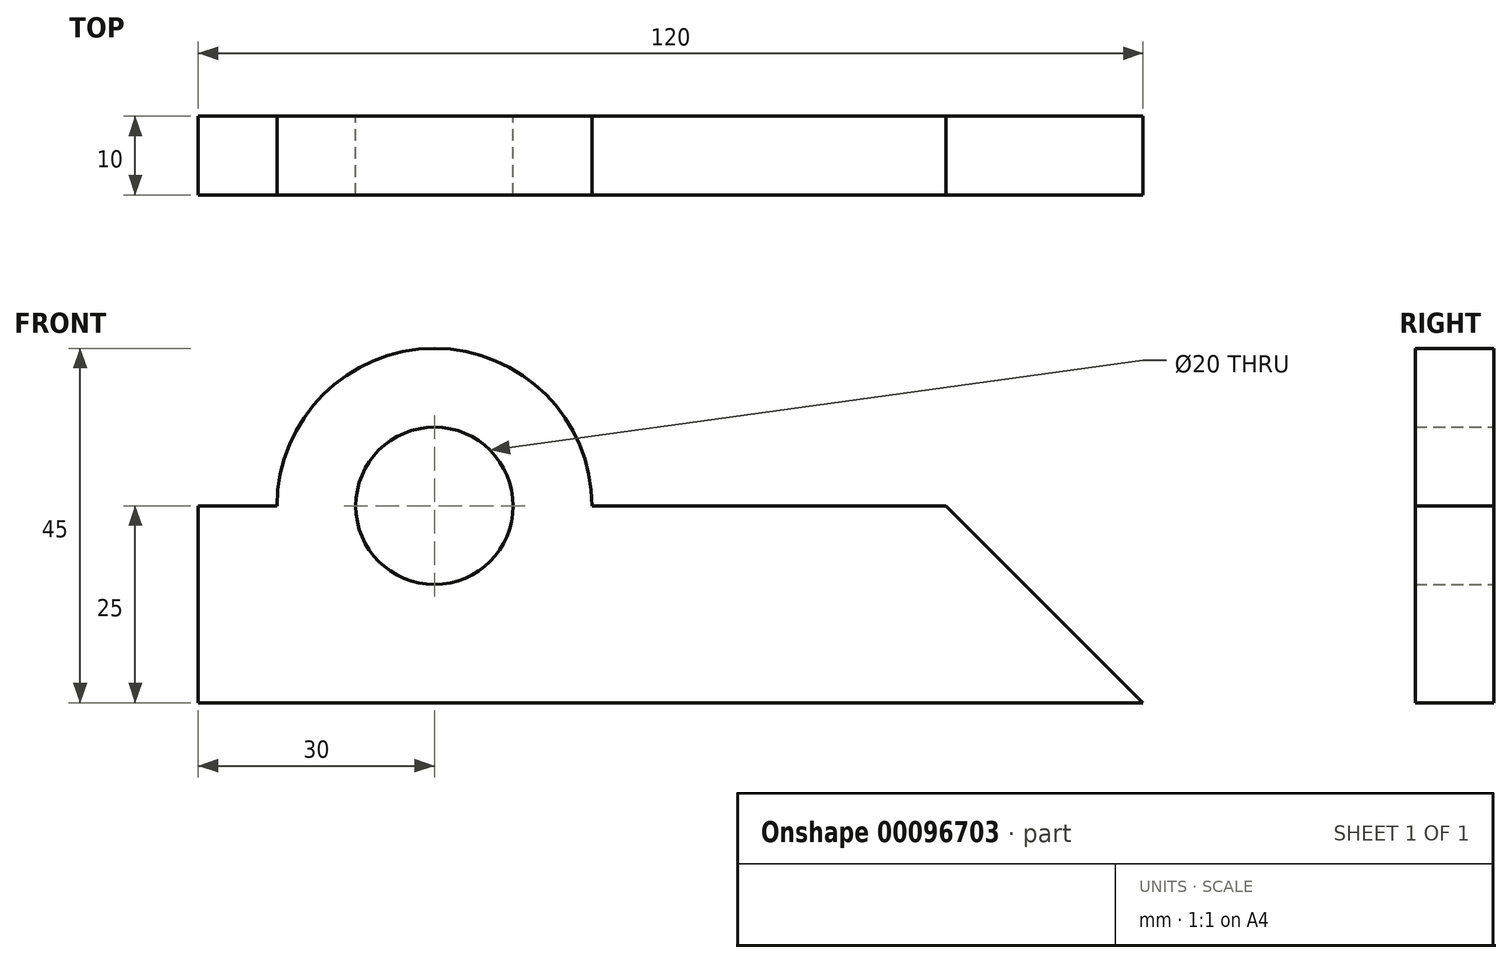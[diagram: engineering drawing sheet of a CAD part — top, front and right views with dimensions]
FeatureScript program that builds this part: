
annotation { "Feature Type Name" : "Feature", "Feature Type Description" : "" }
export const myFeature = defineFeature(function(context is Context, id is Id, definition is map)
    precondition{}
    {
        {
            var Q0;
            Q0=qCreatedBy(makeId("Front.planeOp"),FACE);
            var sketch = newSketch(context, id + "F0", { "sketchPlane" : qUnion([Q0])});
            skLineSegment(sketch, "E0", {"start": v(0, 0) * mm, "end": v(0, 25) * mm});
            skLineSegment(sketch, "E1", {"start": v(0, 25) * mm, "end": v(0, 0) * mm});
            skLineSegment(sketch, "E2", {"start": v(120, 0) * mm, "end": v(95, 25) * mm});
            skLineSegment(sketch, "E3", {"start": v(95, 25) * mm, "end": v(50, 25) * mm});
            skLineSegment(sketch, "E4", {"start": v(0, 25) * mm, "end": v(10, 25) * mm});
            skArc(sketch, "E5", {"start": v(50, 25) * mm, "mid": v(30, 45) * mm, "end": v(10, 25) * mm});
            skLineSegment(sketch, "E6", {"start": v(0, 0) * mm, "end": v(120, 0) * mm});
            skCircle(sketch, "E7", {"center": v(30, 25) * mm, "radius": 10 * mm});
            skSolve(sketch);
        }
        {
            var Q0;
            Q0 = qSketchRegion(id + "F0", true);
            extrude(context, id + "F1", {"entities" : qUnion([Q0]), "depth" : 10 * mm});
        }
    });
